# Revit family: VRF_MML1BH_07-12_Indoor Unit
name_source: partatom
category: Mechanical Equipment
revit_build: Autodesk Revit 2017 (Build: 20160225_1515(x64)
units: mm (PartAtom-declared; Revit-internal decimal feet)

## family parameters
Always vertical = Yes
Cut with Voids When Loaded = No
OmniClass Number = 23.75.00.00
OmniClass Title = Climate Control (HVAC)
Part Type = Breaks Into
Room Calculation Point = No
Round Connector Dimension = Use Diameter
Shared = No
Work Plane-Based = No

## types (3) — shared parameters
Airflow m3/h- High = 460
Airflow m3/h- Low = 300
Airflow m3/h- Mid = 400
Article Description = Console concealed
Capacity = -
Compressor detail-Motor output kW = -
Compressor detail-Type = -
Connectivity = -
Content Supplier URL = www.hcltech.com
Custom = Yes
Depth (mm) = 220 mm  [stored 0.721785 ft]
Description = Console concealed
Drain pipe(mm) = 20
Duct diameters(mm) = -
EMCS = 4
ETIM Article Class = EC001213
Energy class = -
Frequency (Hz) = 50Hz 220-240V
Height (mm) = 600 mm  [stored 1.9685 ft]
MCA (A) = 0.36
MEPcontent Class = HEATPUMP
MOCP (A) = 15
Manufacturer = Toshiba
Manufacturer URL = https://www.toshiba-carrier.co.jp
Part Load = -
Piping diameter Gas (mm) = 10 mm  [stored 0.0328084 ft]
Piping diameter Liquid (mm) = 6 mm  [stored 0.019685 ft]
Power Consumption W- High = 56
Power Consumption W- Low = 39
Power Consumption W- Mid = 50
Power consumption-Cooling (Kw) = 0.056
Power consumption-Heating = -
Product Line = TCC
Rated efficiency = -
Red = Colour RGB-255 000 000
Refrigerant information = R410A
Running current-Cooling (A) = 0.25
Running current-Heating = -
Seasonal and Rated Efficiency = -
Sound pressure  (dB)- High = 36
Sound pressure  (dB)- Mid = 34
Sound pressure (dB)- Low = 32
Starting current = 0.60
URL = https://www.toshiba-carrier.co.jp
Voltage (V) = 60Hz 220V
Weight (Kg) = 21
White = Colour RGB-255 255 255
Width (mm) = 735 mm

## per-type parameters (varying)
| type | Capacities KW - Cooling | Capacities KW - Heating | Static pressure Pa |
| MML-UP0071BH-E | 2.2 | 2.5 | - |
| MML-UP0091BH-E | 2.8 | 3.2 | - |
| MML-UP0121BH-E | 3.6 | 4 | 0 |

note: column(s) folded — value = type name in every type: Article Type, Manufacturer Art. No., Model

note: [stored X ft] marks values corroborated as IEEE doubles in the binary element streams (Revit-internal decimal feet)

## geometry (parser evidence)
native form markers: Sweep x5
no freeform markers — native parametric forms only
